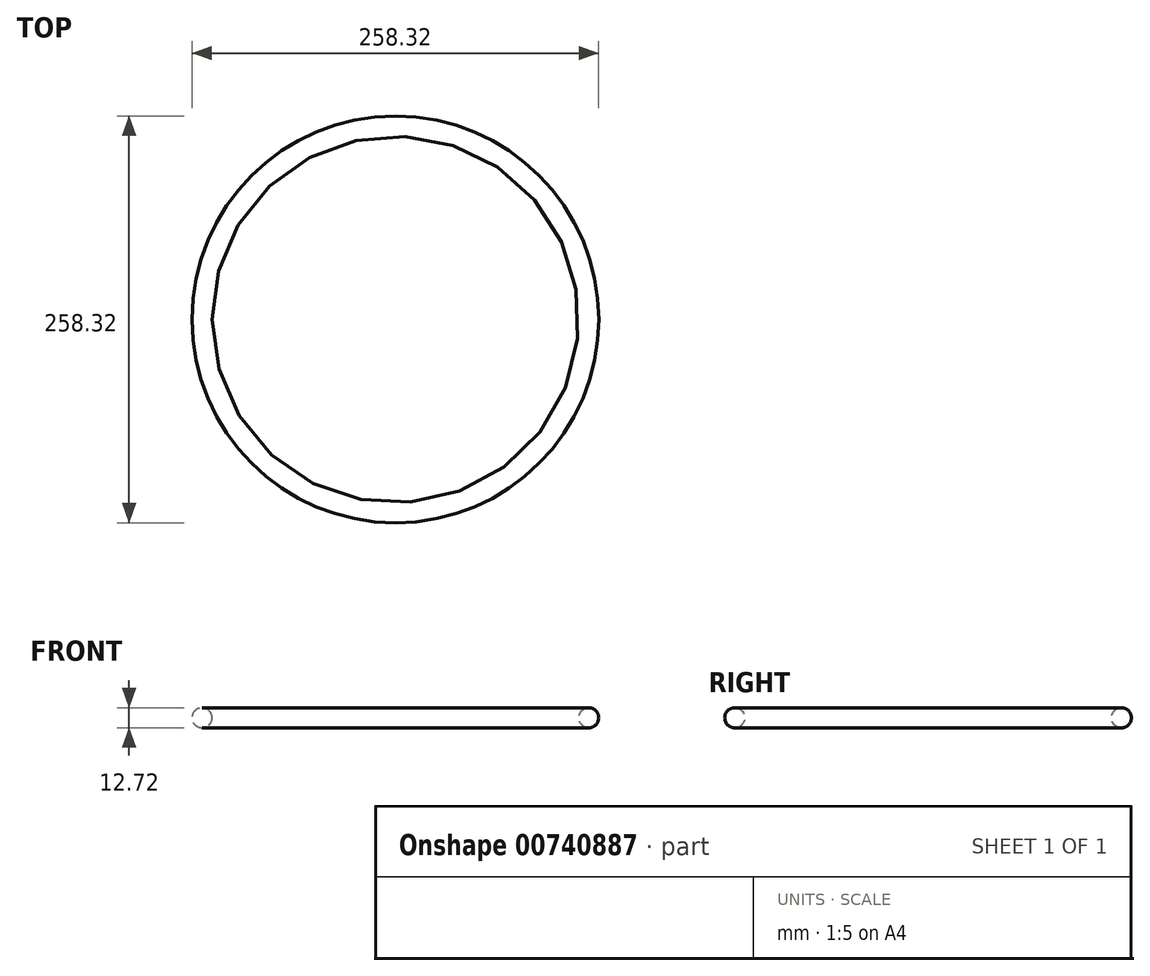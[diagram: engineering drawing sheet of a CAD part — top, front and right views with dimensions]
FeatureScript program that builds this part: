
annotation { "Feature Type Name" : "Feature", "Feature Type Description" : "" }
export const myFeature = defineFeature(function(context is Context, id is Id, definition is map)
    precondition{}
    {
        {
            var Q0;
            Q0=qCreatedBy(makeId("Front.planeOp"),FACE);
            var sketch = newSketch(context, id + "F0", { "sketchPlane" : qUnion([Q0])});
            skCircle(sketch, "E0", {"center": v(-122.8, 0) * mm, "radius": 6.36 * mm});
            skLineSegment(sketch, "E1", {"start": v(0, 0) * mm, "end": v(0, 76.32) * mm});
            skSolve(sketch);
        }
        {
            var Q0;
            Q0=makeQuery(id+"F0.imprint","IMPRINT",FACE,{"disambiguationData":[TD([[makeQuery(id+"F0.imprint","IMPRINT",EDGE,{"derivedFrom":sQuery(id+"F0.wireOp",EDGE,"E0")}),1.0]])]});
            var Q1;
            Q1=sQuery(id+"F0.wireOp",EDGE,"E1");
            revolve(context, id + "F1", {"surfaceOperationType" : NewSurfaceOperationType.NEW, "entities" : qUnion([Q0]), "axis" : qUnion([Q1]), "revolveType" : RevolveType.FULL});
        }
    });
